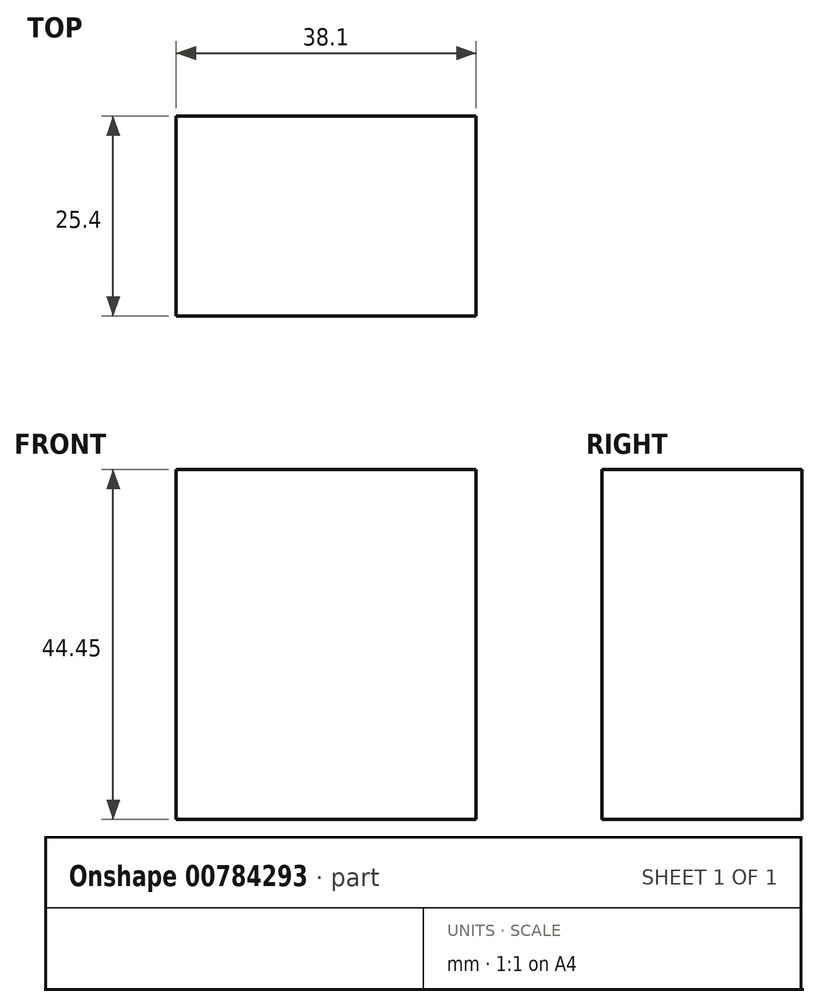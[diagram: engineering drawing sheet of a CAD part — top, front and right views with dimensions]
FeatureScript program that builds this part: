
annotation { "Feature Type Name" : "Feature", "Feature Type Description" : "" }
export const myFeature = defineFeature(function(context is Context, id is Id, definition is map)
    precondition{}
    {
        {
            var Q0;
            Q0=qCreatedBy(makeId("Front.planeOp"),FACE);
            var sketch = newSketch(context, id + "F0", { "sketchPlane" : qUnion([Q0])});
            skLineSegment(sketch, "E0", {"start": v(0, 0) * mm, "end": v(38.1, 0) * mm});
            skLineSegment(sketch, "E1", {"start": v(38.1, 0) * mm, "end": v(38.1, 44.45) * mm});
            skLineSegment(sketch, "E2", {"start": v(38.1, 44.45) * mm, "end": v(0, 44.45) * mm});
            skLineSegment(sketch, "E3", {"start": v(0, 44.45) * mm, "end": v(0, 0) * mm});
            skSolve(sketch);
        }
        {
            var Q0;
            Q0=makeQuery(id+"F0.imprint","IMPRINT",FACE,{"disambiguationData":[TD([[makeQuery(id+"F0.imprint","IMPRINT",EDGE,{"derivedFrom":sQuery(id+"F0.wireOp",EDGE,"E0")}),1.0]])]});
            extrude(context, id + "F1", {"entities" : qUnion([Q0]), "depth" : 25.4 * mm, "offsetDistance" : 25.4 * mm});
        }
    });
